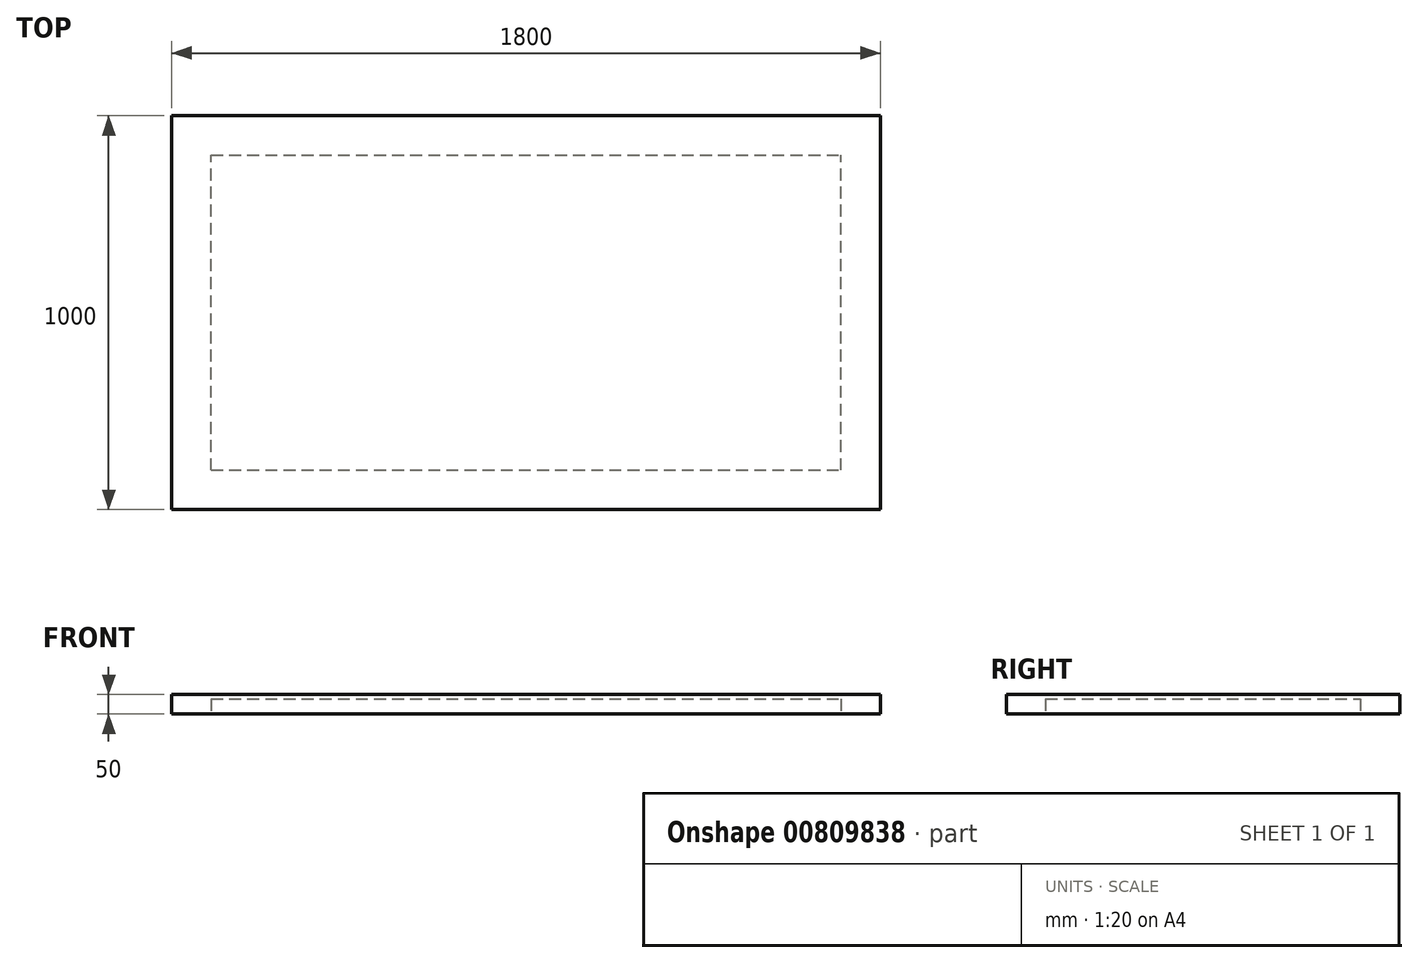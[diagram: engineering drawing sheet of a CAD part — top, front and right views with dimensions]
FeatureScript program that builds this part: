
annotation { "Feature Type Name" : "Feature", "Feature Type Description" : "" }
export const myFeature = defineFeature(function(context is Context, id is Id, definition is map)
    precondition{}
    {
        {
            var Q0;
            Q0=qCreatedBy(makeId("Top.planeOp"),FACE);
            var sketch = newSketch(context, id + "F0", { "sketchPlane" : qUnion([Q0])});
            skLineSegment(sketch, "E0.bottom", {"start": v(-900, -500) * mm, "end": v(900, -500) * mm});
            skLineSegment(sketch, "E0.top", {"start": v(-900, 500) * mm, "end": v(900, 500) * mm});
            skLineSegment(sketch, "E0.left", {"start": v(-900, -500) * mm, "end": v(-900, 500) * mm});
            skLineSegment(sketch, "E0.right", {"start": v(900, -500) * mm, "end": v(900, 500) * mm});
            skPoint(sketch, "E0.middle", {"position": v(0, 0) * mm});
            skSolve(sketch);
        }
        {
            var Q0;
            Q0 = qSketchRegion(id + "F0", true);
            extrude(context, id + "F1", {"entities" : qUnion([Q0]), "depth" : 50 * mm, "offsetDistance" : 25 * mm});
        }
        {
            var Q0;
            Q0=makeQuery(id+"F1.opExtrude","CAP_FACE",FACE,{"disambiguationData":[OSD([sQuery(id+"F0.wireOp",EDGE,"E0.bottom"),sQuery(id+"F0.wireOp",EDGE,"E0.top"),sQuery(id+"F0.wireOp",EDGE,"E0.left"),sQuery(id+"F0.wireOp",EDGE,"E0.right")])],"isStart":true});
            var sketch = newSketch(context, id + "F2", { "sketchPlane" : qUnion([Q0])});
            skLineSegment(sketch, "E1.bottom", {"start": v(-800, 400) * mm, "end": v(800, 400) * mm});
            skLineSegment(sketch, "E1.top", {"start": v(-800, -400) * mm, "end": v(800, -400) * mm});
            skLineSegment(sketch, "E1.left", {"start": v(-800, 400) * mm, "end": v(-800, -400) * mm});
            skLineSegment(sketch, "E1.right", {"start": v(800, 400) * mm, "end": v(800, -400) * mm});
            skPoint(sketch, "E1.middle", {"position": v(0, 0) * mm});
            skSolve(sketch);
        }
        {
            var Q0;
            Q0 = qSketchRegion(id + "F2", true);
            extrude(context, id + "F3", {"entities" : qUnion([Q0]), "operationType" : NewBodyOperationType.REMOVE, "oppositeDirection" : true, "depth" : 38.07 * mm, "offsetDistance" : 25 * mm});
        }
    });
